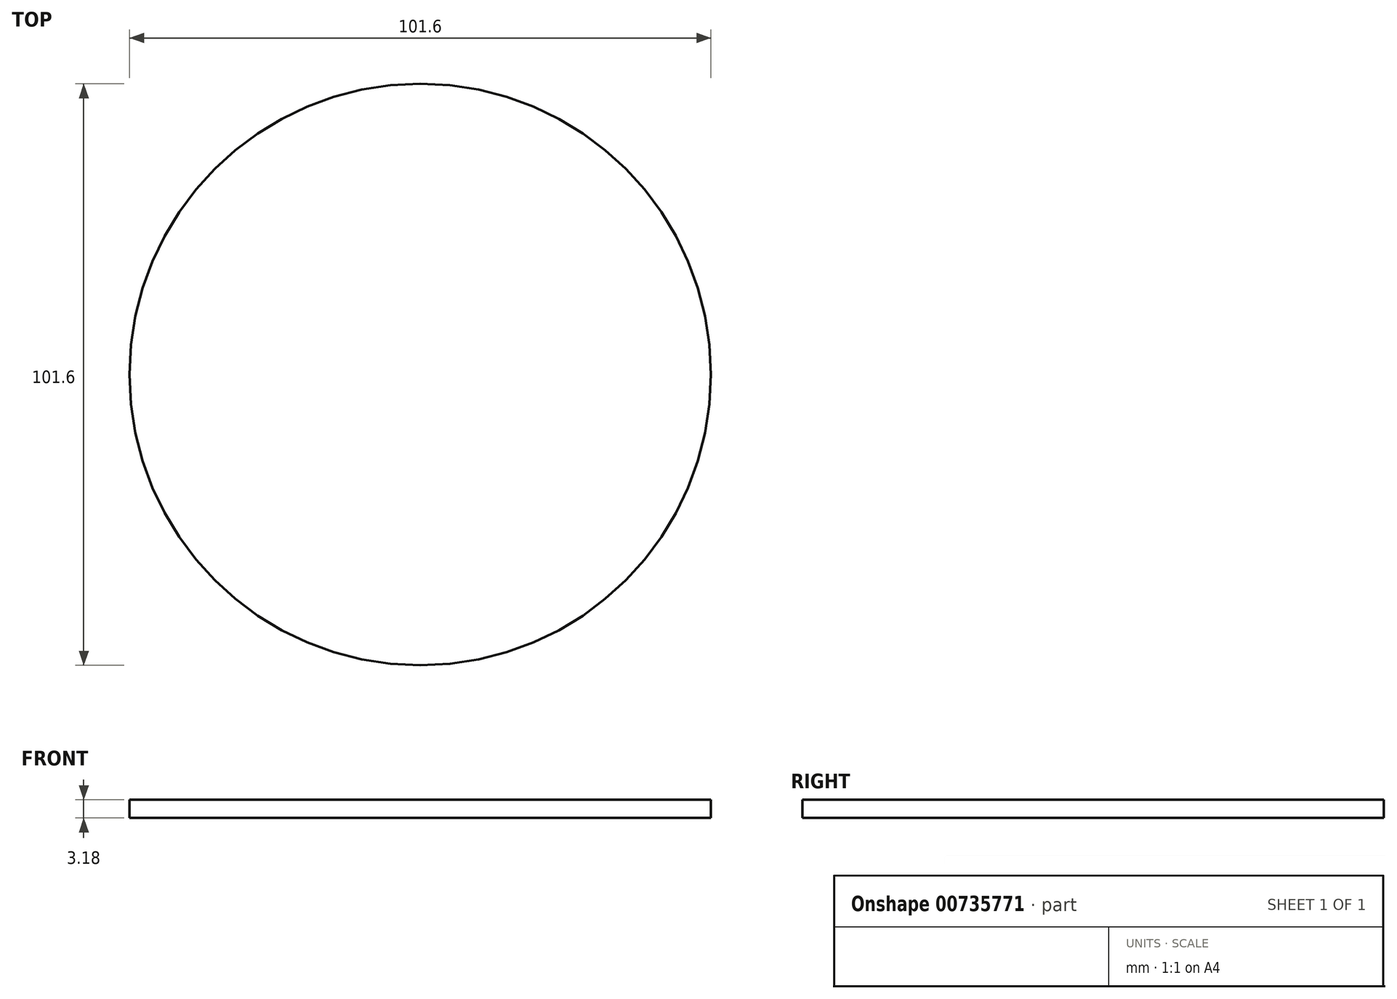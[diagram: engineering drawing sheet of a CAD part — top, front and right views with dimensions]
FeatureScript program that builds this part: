
annotation { "Feature Type Name" : "Feature", "Feature Type Description" : "" }
export const myFeature = defineFeature(function(context is Context, id is Id, definition is map)
    precondition{}
    {
        {
            var Q0;
            Q0=qCreatedBy(makeId("Top.planeOp"),FACE);
            var sketch = newSketch(context, id + "F0", { "sketchPlane" : qUnion([Q0])});
            skCircle(sketch, "E0", {"center": v(0, 0) * mm, "radius": 50.8 * mm});
            skSolve(sketch);
        }
        {
            var Q0;
            Q0=makeQuery(id+"F0.imprint","IMPRINT",FACE,{"disambiguationData":[TD([[makeQuery(id+"F0.imprint","IMPRINT",EDGE,{"derivedFrom":sQuery(id+"F0.wireOp",EDGE,"E0")}),1.0]])]});
            extrude(context, id + "F1", {"entities" : qUnion([Q0]), "depth" : 3.17 * mm, "offsetDistance" : 25.4 * mm});
        }
    });
